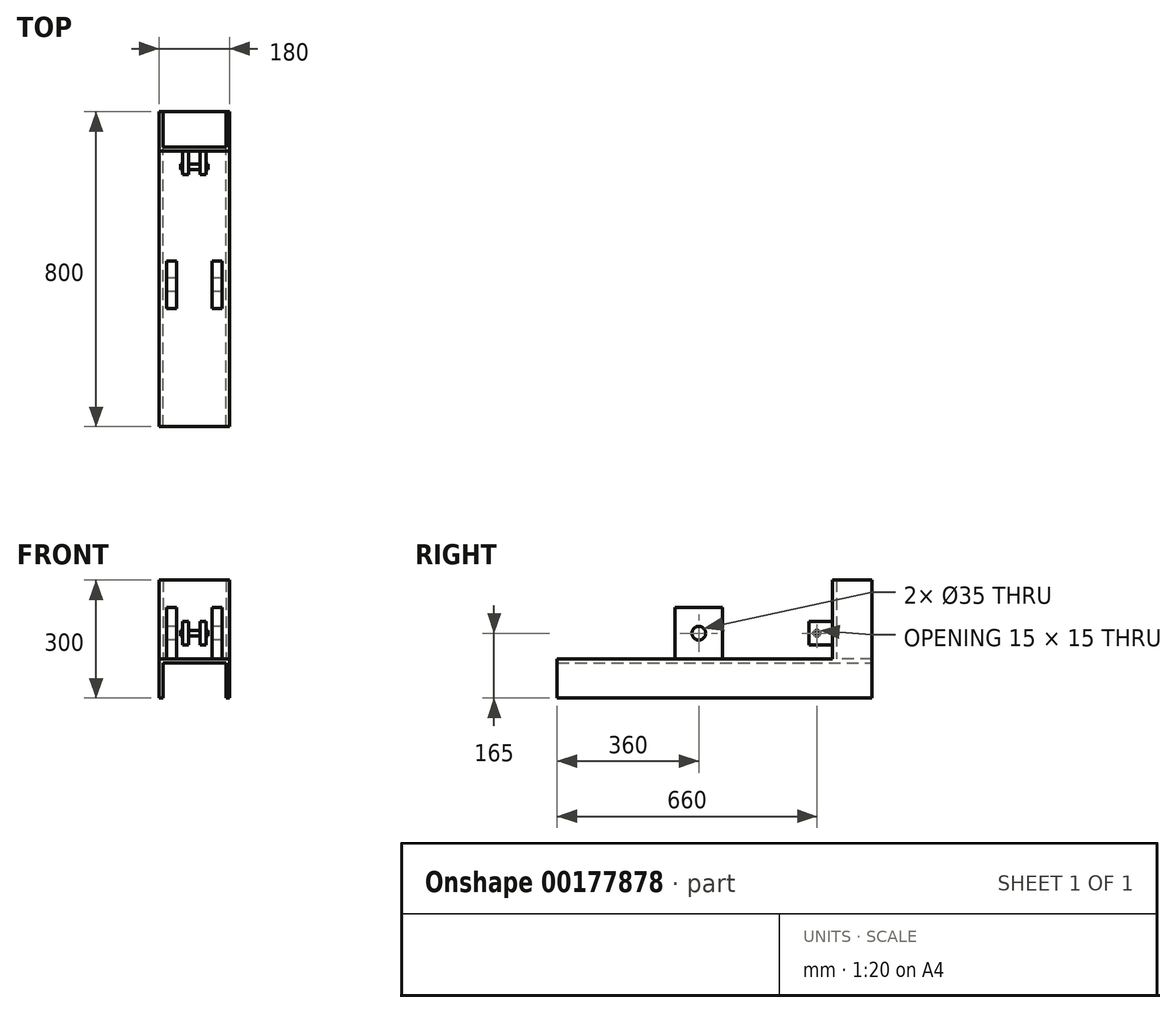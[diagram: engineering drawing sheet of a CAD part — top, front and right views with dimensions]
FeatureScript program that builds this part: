
annotation { "Feature Type Name" : "Feature", "Feature Type Description" : "" }
export const myFeature = defineFeature(function(context is Context, id is Id, definition is map)
    precondition{}
    {
        {
            var Q0;
            Q0=qCreatedBy(makeId("Front.planeOp"),FACE);
            var sketch = newSketch(context, id + "F0", { "sketchPlane" : qUnion([Q0])});
            skLineSegment(sketch, "E0.bottom", {"start": v(0, 0) * mm, "end": v(10, 0) * mm});
            skLineSegment(sketch, "E0.top", {"start": v(0, 100) * mm, "end": v(180, 100) * mm});
            skLineSegment(sketch, "E0.left", {"start": v(0, 0) * mm, "end": v(0, 100) * mm});
            skLineSegment(sketch, "E0.right", {"start": v(180, 0) * mm, "end": v(180, 100) * mm});
            skLineSegment(sketch, "E1.top", {"start": v(10, 90) * mm, "end": v(170, 90) * mm});
            skLineSegment(sketch, "E1.left", {"start": v(10, 0) * mm, "end": v(10, 90) * mm});
            skLineSegment(sketch, "E1.right", {"start": v(170, 0) * mm, "end": v(170, 90) * mm});
            skLineSegment(sketch, "E2.trimOffspring", {"start": v(170, 0) * mm, "end": v(180, 0) * mm});
            skSolve(sketch);
        }
        {
            var Q0;
            Q0=makeQuery(id+"F0.imprint","IMPRINT",FACE,{"disambiguationData":[TD([[makeQuery(id+"F0.imprint","IMPRINT",EDGE,{"derivedFrom":sQuery(id+"F0.wireOp",EDGE,"E0.bottom")}),1.0]])]});
            extrude(context, id + "F1", {"entities" : qUnion([Q0]), "depth" : 800 * mm});
        }
        {
            var Q0;
            Q0=makeQuery(id+"F1.opExtrude","SWEPT_FACE",FACE,{"disambiguationData":[OSD([sQuery(id+"F0.wireOp",EDGE,"E0.top")])]});
            var sketch = newSketch(context, id + "F2", { "sketchPlane" : qUnion([Q0])});
            skLineSegment(sketch, "E3.bottom", {"start": v(0, 0) * mm, "end": v(10, 0) * mm});
            skLineSegment(sketch, "E3.top", {"start": v(0, -100) * mm, "end": v(180, -100) * mm});
            skLineSegment(sketch, "E3.left", {"start": v(0, 0) * mm, "end": v(0, -100) * mm});
            skLineSegment(sketch, "E3.right", {"start": v(180, 0) * mm, "end": v(180, -100) * mm});
            skLineSegment(sketch, "E4.top", {"start": v(10, -90) * mm, "end": v(170, -90) * mm});
            skLineSegment(sketch, "E4.left", {"start": v(10, 0) * mm, "end": v(10, -90) * mm});
            skLineSegment(sketch, "E4.right", {"start": v(170, 0) * mm, "end": v(170, -90) * mm});
            skLineSegment(sketch, "E5.trimOffspring", {"start": v(170, 0) * mm, "end": v(180, 0) * mm});
            skSolve(sketch);
        }
        {
            var Q0;
            Q0=makeQuery(id+"F2.imprint","IMPRINT",FACE,{"disambiguationData":[TD([[makeQuery(id+"F2.imprint","IMPRINT",EDGE,{"derivedFrom":sQuery(id+"F2.wireOp",EDGE,"E3.bottom")}),-1.0]])]});
            extrude(context, id + "F3", {"entities" : qUnion([Q0]), "operationType" : NewBodyOperationType.ADD, "depth" : 200 * mm});
        }
        {
            var Q0;
            {var subQ1=sQuery(id+"F0.wireOp",EDGE,"E0.left");var subQ2=sQuery(id+"F0.wireOp",EDGE,"E0.top");Q0=makeQuery(id+"F3.boolean.opBoolean","SPLIT",FACE,{"disambiguationData":[TD([makeQuery(id+"F1.opExtrude","SWEPT_FACE",FACE,{"disambiguationData":[OSD([subQ1])]})])],"derivedFrom":makeQuery(id+"F1.opExtrude","SWEPT_FACE",FACE,{"disambiguationData":[OSD([subQ2])]})});}
            var sketch = newSketch(context, id + "F4", { "sketchPlane" : qUnion([Q0])});
            skLineSegment(sketch, "E6.bottom", {"start": v(0, -380) * mm, "end": v(45, -380) * mm});
            skLineSegment(sketch, "E6.top", {"start": v(0, -500) * mm, "end": v(45, -500) * mm});
            skLineSegment(sketch, "E6.left", {"start": v(0, -380) * mm, "end": v(0, -500) * mm});
            skLineSegment(sketch, "E6.right", {"start": v(45, -380) * mm, "end": v(45, -500) * mm});
            skLineSegment(sketch, "E7.bottom", {"start": v(180, -380) * mm, "end": v(135, -380) * mm});
            skLineSegment(sketch, "E7.top", {"start": v(180, -500) * mm, "end": v(135, -500) * mm});
            skLineSegment(sketch, "E7.left", {"start": v(180, -380) * mm, "end": v(180, -500) * mm});
            skLineSegment(sketch, "E7.right", {"start": v(135, -380) * mm, "end": v(135, -500) * mm});
            skLineSegment(sketch, "E8", {"start": v(20, -380) * mm, "end": v(20, -500) * mm});
            skLineSegment(sketch, "E9", {"start": v(160, -380) * mm, "end": v(160, -500) * mm});
            skSolve(sketch);
        }
        {
            var Q0;
            {var subQ0=sQuery(id+"F4.wireOp",EDGE,"E6.right");Q0=makeQuery(id+"F4.imprint","IMPRINT",FACE,{"disambiguationData":[TD([[makeQuery(id+"F4.imprint","IMPRINT",EDGE,{"derivedFrom":subQ0}),-1.0]])]});}
            var Q1;
            {var subQ0=sQuery(id+"F4.wireOp",EDGE,"E7.right");Q1=makeQuery(id+"F4.imprint","IMPRINT",FACE,{"disambiguationData":[TD([[makeQuery(id+"F4.imprint","IMPRINT",EDGE,{"derivedFrom":subQ0}),1.0]])]});}
            extrude(context, id + "F5", {"entities" : qUnion([Q0, Q1]), "operationType" : NewBodyOperationType.ADD, "depth" : 130 * mm});
        }
        {
            var Q0;
            Q0=makeQuery(id+"F3.opExtrude","SWEPT_FACE",FACE,{"disambiguationData":[OSD([sQuery(id+"F2.wireOp",EDGE,"E3.top")])]});
            var sketch = newSketch(context, id + "F6", { "sketchPlane" : qUnion([Q0])});
            skLineSegment(sketch, "E10.bottom", {"start": v(60, 195) * mm, "end": v(75, 195) * mm});
            skLineSegment(sketch, "E10.top", {"start": v(60, 135) * mm, "end": v(75, 135) * mm});
            skLineSegment(sketch, "E10.left", {"start": v(60, 195) * mm, "end": v(60, 135) * mm});
            skLineSegment(sketch, "E10.right", {"start": v(75, 195) * mm, "end": v(75, 135) * mm});
            skLineSegment(sketch, "E11.bottom", {"start": v(105, 195) * mm, "end": v(120, 195) * mm});
            skLineSegment(sketch, "E11.top", {"start": v(105, 135) * mm, "end": v(120, 135) * mm});
            skLineSegment(sketch, "E11.left", {"start": v(105, 195) * mm, "end": v(105, 135) * mm});
            skLineSegment(sketch, "E11.right", {"start": v(120, 195) * mm, "end": v(120, 135) * mm});
            skSolve(sketch);
        }
        {
            var Q0;
            Q0=makeQuery(id+"F6.imprint","IMPRINT",FACE,{"disambiguationData":[TD([[makeQuery(id+"F6.imprint","IMPRINT",EDGE,{"derivedFrom":sQuery(id+"F6.wireOp",EDGE,"E10.bottom")}),-1.0]])]});
            var Q1;
            Q1=makeQuery(id+"F6.imprint","IMPRINT",FACE,{"disambiguationData":[TD([[makeQuery(id+"F6.imprint","IMPRINT",EDGE,{"derivedFrom":sQuery(id+"F6.wireOp",EDGE,"E11.bottom")}),-1.0]])]});
            extrude(context, id + "F7", {"entities" : qUnion([Q0, Q1]), "operationType" : NewBodyOperationType.ADD, "depth" : 60 * mm});
        }
        {
            var Q0;
            Q0=makeQuery(id+"F7.opExtrude","SWEPT_FACE",FACE,{"disambiguationData":[OSD([sQuery(id+"F6.wireOp",EDGE,"E10.left")])]});
            var sketch = newSketch(context, id + "F8", { "sketchPlane" : qUnion([Q0])});
            skCircle(sketch, "E12", {"center": v(140, 165) * mm, "radius": 7.5 * mm});
            skPoint(sketch, "E12.centerSnap0", {"position": v(160, 165) * mm});
            skSolve(sketch);
        }
        {
            var Q0;
            Q0=makeQuery(id+"F8.imprint","IMPRINT",FACE,{"disambiguationData":[TD([[makeQuery(id+"F8.imprint","IMPRINT",EDGE,{"derivedFrom":sQuery(id+"F8.wireOp",EDGE,"E12")}),1.0]])]});
            extrude(context, id + "F9", {"entities" : qUnion([Q0]), "operationType" : NewBodyOperationType.ADD, "oppositeDirection" : true, "depth" : 65 * mm, "hasSecondDirection" : true, "secondDirectionOppositeDirection" : false, "secondDirectionDepth" : 5 * mm});
        }
        {
            var Q0;
            Q0=makeQuery(id+"F5.opExtrude","SWEPT_FACE",FACE,{"disambiguationData":[OSD([sQuery(id+"F4.wireOp",EDGE,"E8")])]});
            var sketch = newSketch(context, id + "F10", { "sketchPlane" : qUnion([Q0])});
            skCircle(sketch, "E13", {"center": v(440, 165) * mm, "radius": 17.5 * mm});
            skSolve(sketch);
        }
        {
            var Q0;
            Q0 = qSketchRegion(id + "F10", true);
            extrude(context, id + "F11", {"entities" : qUnion([Q0]), "operationType" : NewBodyOperationType.REMOVE, "endBound" : BoundingType.THROUGH_ALL, "oppositeDirection" : true, "depth" : 25 * mm});
        }
    });
